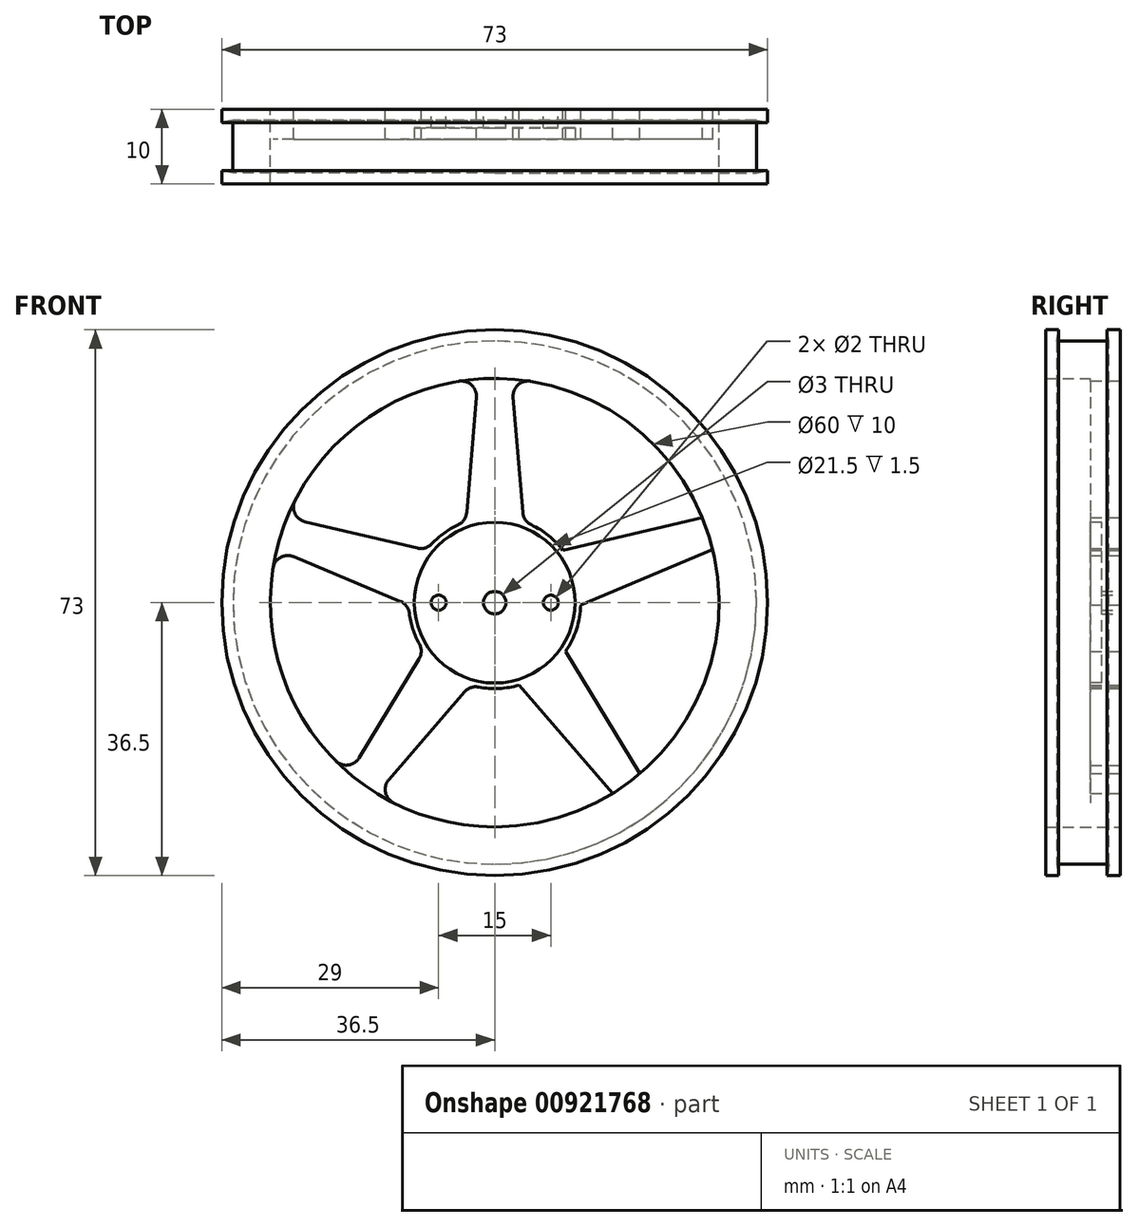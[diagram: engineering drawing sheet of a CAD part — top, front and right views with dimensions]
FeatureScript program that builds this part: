
annotation { "Feature Type Name" : "Feature", "Feature Type Description" : "" }
export const myFeature = defineFeature(function(context is Context, id is Id, definition is map)
    precondition{}
    {
        {
            var Q0;
            Q0=qCreatedBy(makeId("Front.planeOp"),FACE);
            var sketch = newSketch(context, id + "F0", { "sketchPlane" : qUnion([Q0])});
            skCircle(sketch, "E0", {"center": v(0, 0) * mm, "radius": 36.5 * mm});
            skCircle(sketch, "E1", {"center": v(0, 0) * mm, "radius": 30 * mm});
            skSolve(sketch);
        }
        {
            var Q0;
            Q0 = qSketchRegion(id + "F0", true);
            extrude(context, id + "F1", {"entities" : qUnion([Q0]), "depth" : 10 * mm, "offsetDistance" : 25 * mm});
        }
        {
            var Q0;
            Q0=qCreatedBy(makeId("Front.planeOp"),FACE);
            var sketch = newSketch(context, id + "F2", { "sketchPlane" : qUnion([Q0])});
            skCircle(sketch, "E2", {"center": v(0, 0) * mm, "radius": 11.5 * mm});
            skCircle(sketch, "E3", {"center": v(0, 0) * mm, "radius": 1.5 * mm});
            skCircle(sketch, "E4", {"center": v(-7.5, 0) * mm, "radius": 1 * mm});
            skCircle(sketch, "E5", {"center": v(7.5, 0) * mm, "radius": 1 * mm});
            skSolve(sketch);
        }
        {
            var Q0;
            Q0=makeQuery(id+"F2.imprint","IMPRINT",FACE,{"disambiguationData":[TD([[makeQuery(id+"F2.imprint","IMPRINT",EDGE,{"derivedFrom":sQuery(id+"F2.wireOp",EDGE,"E2")}),1.0]])]});
            extrude(context, id + "F3", {"entities" : qUnion([Q0]), "operationType" : NewBodyOperationType.ADD, "depth" : 4 * mm, "offsetDistance" : 25 * mm});
        }
        {
            var Q0;
            Q0=qCreatedBy(makeId("Front.planeOp"),FACE);
            var sketch = newSketch(context, id + "F4", { "sketchPlane" : qUnion([Q0])});
            skLineSegment(sketch, "E6", {"start": v(-4, 9) * mm, "end": v(4, 9) * mm});
            skLineSegment(sketch, "E7", {"start": v(2, 33) * mm, "end": v(-2, 33) * mm});
            skLineSegment(sketch, "E8", {"start": v(-2, 33) * mm, "end": v(-4, 9) * mm});
            skLineSegment(sketch, "E9", {"start": v(2, 33) * mm, "end": v(4, 9) * mm});
            skLineSegment(sketch, "E10.1.0", {"start": v(-32, 8.3) * mm, "end": v(-9.8, -1.02) * mm});
            skLineSegment(sketch, "E10.1.1", {"start": v(-30.77, 12.1) * mm, "end": v(-32, 8.3) * mm});
            skLineSegment(sketch, "E10.1.2", {"start": v(-30.77, 12.1) * mm, "end": v(-7.32, 6.59) * mm});
            skLineSegment(sketch, "E10.1.3", {"start": v(-9.8, -1.02) * mm, "end": v(-7.32, 6.59) * mm});
            skLineSegment(sketch, "E10.2.0", {"start": v(-17.78, -27.87) * mm, "end": v(-2.05, -9.63) * mm});
            skLineSegment(sketch, "E10.2.1", {"start": v(-21.01, -25.52) * mm, "end": v(-17.78, -27.87) * mm});
            skLineSegment(sketch, "E10.2.2", {"start": v(-21.01, -25.52) * mm, "end": v(-8.53, -4.93) * mm});
            skLineSegment(sketch, "E10.2.3", {"start": v(-2.05, -9.63) * mm, "end": v(-8.53, -4.93) * mm});
            skPoint(sketch, "E10.center", {"position": v(0, 0) * mm});
            skLineSegment(sketch, "E11.2.3.0", {"start": v(21.01, -25.52) * mm, "end": v(8.53, -4.93) * mm});
            skLineSegment(sketch, "E11.3.3.0", {"start": v(17.78, -27.87) * mm, "end": v(21.01, -25.52) * mm});
            skLineSegment(sketch, "E11.6.3.0", {"start": v(17.78, -27.87) * mm, "end": v(2.05, -9.63) * mm});
            skLineSegment(sketch, "E11.9.3.0", {"start": v(8.53, -4.93) * mm, "end": v(2.05, -9.63) * mm});
            skLineSegment(sketch, "E12.2.4.0", {"start": v(30.77, 12.1) * mm, "end": v(7.32, 6.59) * mm});
            skLineSegment(sketch, "E12.3.4.0", {"start": v(32, 8.3) * mm, "end": v(30.77, 12.1) * mm});
            skLineSegment(sketch, "E12.6.4.0", {"start": v(32, 8.3) * mm, "end": v(9.8, -1.02) * mm});
            skLineSegment(sketch, "E12.9.4.0", {"start": v(7.32, 6.59) * mm, "end": v(9.8, -1.02) * mm});
            skSolve(sketch);
        }
        {
            var Q0;
            Q0 = qSketchRegion(id + "F4", true);
            extrude(context, id + "F5", {"entities" : qUnion([Q0]), "operationType" : NewBodyOperationType.ADD, "depth" : 4 * mm, "offsetDistance" : 25 * mm});
        }
        {
            var Q0;
            Q0=makeQuery(id+"F5.boolean.opBoolean","INTERSECT",EDGE,{"disambiguationData":[OD(0.0)],"derivedFrom":[makeQuery(id+"F1.opExtrude","SWEPT_FACE",FACE,{"disambiguationData":[OSD([sQuery(id+"F0.wireOp",EDGE,"E1")])]}),makeQuery(id+"F5.opExtrude","CAP_FACE",FACE,{"disambiguationData":[OSD([sQuery(id+"F4.wireOp",EDGE,"E6"),sQuery(id+"F4.wireOp",EDGE,"E7"),sQuery(id+"F4.wireOp",EDGE,"E8"),sQuery(id+"F4.wireOp",EDGE,"E9"),sQuery(id+"F4.wireOp",EDGE,"E10.1.0"),sQuery(id+"F4.wireOp",EDGE,"E10.1.1"),sQuery(id+"F4.wireOp",EDGE,"E10.1.2"),sQuery(id+"F4.wireOp",EDGE,"E10.1.3"),sQuery(id+"F4.wireOp",EDGE,"E10.2.0"),sQuery(id+"F4.wireOp",EDGE,"E10.2.1"),sQuery(id+"F4.wireOp",EDGE,"E10.2.2"),sQuery(id+"F4.wireOp",EDGE,"E10.2.3"),sQuery(id+"F4.wireOp",EDGE,"E10.3.0"),sQuery(id+"F4.wireOp",EDGE,"E10.3.1"),sQuery(id+"F4.wireOp",EDGE,"E10.3.2"),sQuery(id+"F4.wireOp",EDGE,"E10.3.3"),sQuery(id+"F4.wireOp",EDGE,"E10.4.0"),sQuery(id+"F4.wireOp",EDGE,"E10.4.1"),sQuery(id+"F4.wireOp",EDGE,"E10.4.2"),sQuery(id+"F4.wireOp",EDGE,"E10.4.3"),sQuery(id+"F4.wireOp",EDGE,"E10.5.0"),sQuery(id+"F4.wireOp",EDGE,"E10.5.1"),sQuery(id+"F4.wireOp",EDGE,"E10.5.2"),sQuery(id+"F4.wireOp",EDGE,"E10.5.3"),sQuery(id+"F4.wireOp",EDGE,"E10.6.0"),sQuery(id+"F4.wireOp",EDGE,"E10.6.1"),sQuery(id+"F4.wireOp",EDGE,"E10.6.2"),sQuery(id+"F4.wireOp",EDGE,"E10.6.3")])],"isStart":false})]});
            var Q1;
            Q1=makeQuery(id+"F5.boolean.opBoolean","INTERSECT",EDGE,{"disambiguationData":[OD(1.0)],"derivedFrom":[makeQuery(id+"F1.opExtrude","SWEPT_FACE",FACE,{"disambiguationData":[OSD([sQuery(id+"F0.wireOp",EDGE,"E1")])]}),makeQuery(id+"F5.opExtrude","CAP_FACE",FACE,{"disambiguationData":[OSD([sQuery(id+"F4.wireOp",EDGE,"E6"),sQuery(id+"F4.wireOp",EDGE,"E7"),sQuery(id+"F4.wireOp",EDGE,"E8"),sQuery(id+"F4.wireOp",EDGE,"E9"),sQuery(id+"F4.wireOp",EDGE,"E10.1.0"),sQuery(id+"F4.wireOp",EDGE,"E10.1.1"),sQuery(id+"F4.wireOp",EDGE,"E10.1.2"),sQuery(id+"F4.wireOp",EDGE,"E10.1.3"),sQuery(id+"F4.wireOp",EDGE,"E10.2.0"),sQuery(id+"F4.wireOp",EDGE,"E10.2.1"),sQuery(id+"F4.wireOp",EDGE,"E10.2.2"),sQuery(id+"F4.wireOp",EDGE,"E10.2.3"),sQuery(id+"F4.wireOp",EDGE,"E10.3.0"),sQuery(id+"F4.wireOp",EDGE,"E10.3.1"),sQuery(id+"F4.wireOp",EDGE,"E10.3.2"),sQuery(id+"F4.wireOp",EDGE,"E10.3.3"),sQuery(id+"F4.wireOp",EDGE,"E10.4.0"),sQuery(id+"F4.wireOp",EDGE,"E10.4.1"),sQuery(id+"F4.wireOp",EDGE,"E10.4.2"),sQuery(id+"F4.wireOp",EDGE,"E10.4.3"),sQuery(id+"F4.wireOp",EDGE,"E10.5.0"),sQuery(id+"F4.wireOp",EDGE,"E10.5.1"),sQuery(id+"F4.wireOp",EDGE,"E10.5.2"),sQuery(id+"F4.wireOp",EDGE,"E10.5.3"),sQuery(id+"F4.wireOp",EDGE,"E10.6.0"),sQuery(id+"F4.wireOp",EDGE,"E10.6.1"),sQuery(id+"F4.wireOp",EDGE,"E10.6.2"),sQuery(id+"F4.wireOp",EDGE,"E10.6.3")])],"isStart":false})]});
            var Q2;
            Q2=makeQuery(id+"F5.boolean.opBoolean","INTERSECT",EDGE,{"disambiguationData":[OD(2.0)],"derivedFrom":[makeQuery(id+"F1.opExtrude","SWEPT_FACE",FACE,{"disambiguationData":[OSD([sQuery(id+"F0.wireOp",EDGE,"E1")])]}),makeQuery(id+"F5.opExtrude","CAP_FACE",FACE,{"disambiguationData":[OSD([sQuery(id+"F4.wireOp",EDGE,"E6"),sQuery(id+"F4.wireOp",EDGE,"E7"),sQuery(id+"F4.wireOp",EDGE,"E8"),sQuery(id+"F4.wireOp",EDGE,"E9"),sQuery(id+"F4.wireOp",EDGE,"E10.1.0"),sQuery(id+"F4.wireOp",EDGE,"E10.1.1"),sQuery(id+"F4.wireOp",EDGE,"E10.1.2"),sQuery(id+"F4.wireOp",EDGE,"E10.1.3"),sQuery(id+"F4.wireOp",EDGE,"E10.2.0"),sQuery(id+"F4.wireOp",EDGE,"E10.2.1"),sQuery(id+"F4.wireOp",EDGE,"E10.2.2"),sQuery(id+"F4.wireOp",EDGE,"E10.2.3"),sQuery(id+"F4.wireOp",EDGE,"E10.3.0"),sQuery(id+"F4.wireOp",EDGE,"E10.3.1"),sQuery(id+"F4.wireOp",EDGE,"E10.3.2"),sQuery(id+"F4.wireOp",EDGE,"E10.3.3"),sQuery(id+"F4.wireOp",EDGE,"E10.4.0"),sQuery(id+"F4.wireOp",EDGE,"E10.4.1"),sQuery(id+"F4.wireOp",EDGE,"E10.4.2"),sQuery(id+"F4.wireOp",EDGE,"E10.4.3"),sQuery(id+"F4.wireOp",EDGE,"E10.5.0"),sQuery(id+"F4.wireOp",EDGE,"E10.5.1"),sQuery(id+"F4.wireOp",EDGE,"E10.5.2"),sQuery(id+"F4.wireOp",EDGE,"E10.5.3"),sQuery(id+"F4.wireOp",EDGE,"E10.6.0"),sQuery(id+"F4.wireOp",EDGE,"E10.6.1"),sQuery(id+"F4.wireOp",EDGE,"E10.6.2"),sQuery(id+"F4.wireOp",EDGE,"E10.6.3")])],"isStart":false})]});
            var Q3;
            Q3=makeQuery(id+"F5.boolean.opBoolean","INTERSECT",EDGE,{"disambiguationData":[OD(3.0)],"derivedFrom":[makeQuery(id+"F1.opExtrude","SWEPT_FACE",FACE,{"disambiguationData":[OSD([sQuery(id+"F0.wireOp",EDGE,"E1")])]}),makeQuery(id+"F5.opExtrude","CAP_FACE",FACE,{"disambiguationData":[OSD([sQuery(id+"F4.wireOp",EDGE,"E6"),sQuery(id+"F4.wireOp",EDGE,"E7"),sQuery(id+"F4.wireOp",EDGE,"E8"),sQuery(id+"F4.wireOp",EDGE,"E9"),sQuery(id+"F4.wireOp",EDGE,"E10.1.0"),sQuery(id+"F4.wireOp",EDGE,"E10.1.1"),sQuery(id+"F4.wireOp",EDGE,"E10.1.2"),sQuery(id+"F4.wireOp",EDGE,"E10.1.3"),sQuery(id+"F4.wireOp",EDGE,"E10.2.0"),sQuery(id+"F4.wireOp",EDGE,"E10.2.1"),sQuery(id+"F4.wireOp",EDGE,"E10.2.2"),sQuery(id+"F4.wireOp",EDGE,"E10.2.3"),sQuery(id+"F4.wireOp",EDGE,"E10.3.0"),sQuery(id+"F4.wireOp",EDGE,"E10.3.1"),sQuery(id+"F4.wireOp",EDGE,"E10.3.2"),sQuery(id+"F4.wireOp",EDGE,"E10.3.3"),sQuery(id+"F4.wireOp",EDGE,"E10.4.0"),sQuery(id+"F4.wireOp",EDGE,"E10.4.1"),sQuery(id+"F4.wireOp",EDGE,"E10.4.2"),sQuery(id+"F4.wireOp",EDGE,"E10.4.3"),sQuery(id+"F4.wireOp",EDGE,"E10.5.0"),sQuery(id+"F4.wireOp",EDGE,"E10.5.1"),sQuery(id+"F4.wireOp",EDGE,"E10.5.2"),sQuery(id+"F4.wireOp",EDGE,"E10.5.3"),sQuery(id+"F4.wireOp",EDGE,"E10.6.0"),sQuery(id+"F4.wireOp",EDGE,"E10.6.1"),sQuery(id+"F4.wireOp",EDGE,"E10.6.2"),sQuery(id+"F4.wireOp",EDGE,"E10.6.3")])],"isStart":false})]});
            var Q4;
            Q4=makeQuery(id+"F5.boolean.opBoolean","INTERSECT",EDGE,{"disambiguationData":[OD(4.0)],"derivedFrom":[makeQuery(id+"F1.opExtrude","SWEPT_FACE",FACE,{"disambiguationData":[OSD([sQuery(id+"F0.wireOp",EDGE,"E1")])]}),makeQuery(id+"F5.opExtrude","CAP_FACE",FACE,{"disambiguationData":[OSD([sQuery(id+"F4.wireOp",EDGE,"E6"),sQuery(id+"F4.wireOp",EDGE,"E7"),sQuery(id+"F4.wireOp",EDGE,"E8"),sQuery(id+"F4.wireOp",EDGE,"E9"),sQuery(id+"F4.wireOp",EDGE,"E10.1.0"),sQuery(id+"F4.wireOp",EDGE,"E10.1.1"),sQuery(id+"F4.wireOp",EDGE,"E10.1.2"),sQuery(id+"F4.wireOp",EDGE,"E10.1.3"),sQuery(id+"F4.wireOp",EDGE,"E10.2.0"),sQuery(id+"F4.wireOp",EDGE,"E10.2.1"),sQuery(id+"F4.wireOp",EDGE,"E10.2.2"),sQuery(id+"F4.wireOp",EDGE,"E10.2.3"),sQuery(id+"F4.wireOp",EDGE,"E10.3.0"),sQuery(id+"F4.wireOp",EDGE,"E10.3.1"),sQuery(id+"F4.wireOp",EDGE,"E10.3.2"),sQuery(id+"F4.wireOp",EDGE,"E10.3.3"),sQuery(id+"F4.wireOp",EDGE,"E10.4.0"),sQuery(id+"F4.wireOp",EDGE,"E10.4.1"),sQuery(id+"F4.wireOp",EDGE,"E10.4.2"),sQuery(id+"F4.wireOp",EDGE,"E10.4.3"),sQuery(id+"F4.wireOp",EDGE,"E10.5.0"),sQuery(id+"F4.wireOp",EDGE,"E10.5.1"),sQuery(id+"F4.wireOp",EDGE,"E10.5.2"),sQuery(id+"F4.wireOp",EDGE,"E10.5.3"),sQuery(id+"F4.wireOp",EDGE,"E10.6.0"),sQuery(id+"F4.wireOp",EDGE,"E10.6.1"),sQuery(id+"F4.wireOp",EDGE,"E10.6.2"),sQuery(id+"F4.wireOp",EDGE,"E10.6.3")])],"isStart":false})]});
            var Q5;
            Q5=makeQuery(id+"F5.boolean.opBoolean","INTERSECT",EDGE,{"disambiguationData":[OD(5.0)],"derivedFrom":[makeQuery(id+"F1.opExtrude","SWEPT_FACE",FACE,{"disambiguationData":[OSD([sQuery(id+"F0.wireOp",EDGE,"E1")])]}),makeQuery(id+"F5.opExtrude","CAP_FACE",FACE,{"disambiguationData":[OSD([sQuery(id+"F4.wireOp",EDGE,"E6"),sQuery(id+"F4.wireOp",EDGE,"E7"),sQuery(id+"F4.wireOp",EDGE,"E8"),sQuery(id+"F4.wireOp",EDGE,"E9"),sQuery(id+"F4.wireOp",EDGE,"E10.1.0"),sQuery(id+"F4.wireOp",EDGE,"E10.1.1"),sQuery(id+"F4.wireOp",EDGE,"E10.1.2"),sQuery(id+"F4.wireOp",EDGE,"E10.1.3"),sQuery(id+"F4.wireOp",EDGE,"E10.2.0"),sQuery(id+"F4.wireOp",EDGE,"E10.2.1"),sQuery(id+"F4.wireOp",EDGE,"E10.2.2"),sQuery(id+"F4.wireOp",EDGE,"E10.2.3"),sQuery(id+"F4.wireOp",EDGE,"E10.3.0"),sQuery(id+"F4.wireOp",EDGE,"E10.3.1"),sQuery(id+"F4.wireOp",EDGE,"E10.3.2"),sQuery(id+"F4.wireOp",EDGE,"E10.3.3"),sQuery(id+"F4.wireOp",EDGE,"E10.4.0"),sQuery(id+"F4.wireOp",EDGE,"E10.4.1"),sQuery(id+"F4.wireOp",EDGE,"E10.4.2"),sQuery(id+"F4.wireOp",EDGE,"E10.4.3"),sQuery(id+"F4.wireOp",EDGE,"E10.5.0"),sQuery(id+"F4.wireOp",EDGE,"E10.5.1"),sQuery(id+"F4.wireOp",EDGE,"E10.5.2"),sQuery(id+"F4.wireOp",EDGE,"E10.5.3"),sQuery(id+"F4.wireOp",EDGE,"E10.6.0"),sQuery(id+"F4.wireOp",EDGE,"E10.6.1"),sQuery(id+"F4.wireOp",EDGE,"E10.6.2"),sQuery(id+"F4.wireOp",EDGE,"E10.6.3")])],"isStart":false})]});
            var Q6;
            Q6=makeQuery(id+"F5.boolean.opBoolean","INTERSECT",EDGE,{"disambiguationData":[OD(6.0)],"derivedFrom":[makeQuery(id+"F1.opExtrude","SWEPT_FACE",FACE,{"disambiguationData":[OSD([sQuery(id+"F0.wireOp",EDGE,"E1")])]}),makeQuery(id+"F5.opExtrude","CAP_FACE",FACE,{"disambiguationData":[OSD([sQuery(id+"F4.wireOp",EDGE,"E6"),sQuery(id+"F4.wireOp",EDGE,"E7"),sQuery(id+"F4.wireOp",EDGE,"E8"),sQuery(id+"F4.wireOp",EDGE,"E9"),sQuery(id+"F4.wireOp",EDGE,"E10.1.0"),sQuery(id+"F4.wireOp",EDGE,"E10.1.1"),sQuery(id+"F4.wireOp",EDGE,"E10.1.2"),sQuery(id+"F4.wireOp",EDGE,"E10.1.3"),sQuery(id+"F4.wireOp",EDGE,"E10.2.0"),sQuery(id+"F4.wireOp",EDGE,"E10.2.1"),sQuery(id+"F4.wireOp",EDGE,"E10.2.2"),sQuery(id+"F4.wireOp",EDGE,"E10.2.3"),sQuery(id+"F4.wireOp",EDGE,"E10.3.0"),sQuery(id+"F4.wireOp",EDGE,"E10.3.1"),sQuery(id+"F4.wireOp",EDGE,"E10.3.2"),sQuery(id+"F4.wireOp",EDGE,"E10.3.3"),sQuery(id+"F4.wireOp",EDGE,"E10.4.0"),sQuery(id+"F4.wireOp",EDGE,"E10.4.1"),sQuery(id+"F4.wireOp",EDGE,"E10.4.2"),sQuery(id+"F4.wireOp",EDGE,"E10.4.3"),sQuery(id+"F4.wireOp",EDGE,"E10.5.0"),sQuery(id+"F4.wireOp",EDGE,"E10.5.1"),sQuery(id+"F4.wireOp",EDGE,"E10.5.2"),sQuery(id+"F4.wireOp",EDGE,"E10.5.3"),sQuery(id+"F4.wireOp",EDGE,"E10.6.0"),sQuery(id+"F4.wireOp",EDGE,"E10.6.1"),sQuery(id+"F4.wireOp",EDGE,"E10.6.2"),sQuery(id+"F4.wireOp",EDGE,"E10.6.3")])],"isStart":false})]});
            var Q7;
            Q7=makeQuery(id+"F5.boolean.opBoolean","INTERSECT",EDGE,{"derivedFrom":[makeQuery(id+"F1.opExtrude","SWEPT_FACE",FACE,{"disambiguationData":[OSD([sQuery(id+"F0.wireOp",EDGE,"E1")])]}),makeQuery(id+"F5.opExtrude","SWEPT_FACE",FACE,{"disambiguationData":[OSD([sQuery(id+"F4.wireOp",EDGE,"E9")])]})]});
            var Q8;
            Q8=makeQuery(id+"F5.boolean.opBoolean","INTERSECT",EDGE,{"derivedFrom":[makeQuery(id+"F1.opExtrude","SWEPT_FACE",FACE,{"disambiguationData":[OSD([sQuery(id+"F0.wireOp",EDGE,"E1")])]}),makeQuery(id+"F5.opExtrude","SWEPT_FACE",FACE,{"disambiguationData":[OSD([sQuery(id+"F4.wireOp",EDGE,"E8")])]})]});
            var Q9;
            Q9=makeQuery(id+"F5.boolean.opBoolean","INTERSECT",EDGE,{"derivedFrom":[makeQuery(id+"F1.opExtrude","SWEPT_FACE",FACE,{"disambiguationData":[OSD([sQuery(id+"F0.wireOp",EDGE,"E1")])]}),makeQuery(id+"F5.opExtrude","SWEPT_FACE",FACE,{"disambiguationData":[OSD([sQuery(id+"F4.wireOp",EDGE,"E10.6.0")])]})]});
            var Q10;
            Q10=makeQuery(id+"F5.boolean.opBoolean","INTERSECT",EDGE,{"derivedFrom":[makeQuery(id+"F1.opExtrude","SWEPT_FACE",FACE,{"disambiguationData":[OSD([sQuery(id+"F0.wireOp",EDGE,"E1")])]}),makeQuery(id+"F5.opExtrude","SWEPT_FACE",FACE,{"disambiguationData":[OSD([sQuery(id+"F4.wireOp",EDGE,"E10.6.2")])]})]});
            var Q11;
            Q11=makeQuery(id+"F5.boolean.opBoolean","INTERSECT",EDGE,{"derivedFrom":[makeQuery(id+"F1.opExtrude","SWEPT_FACE",FACE,{"disambiguationData":[OSD([sQuery(id+"F0.wireOp",EDGE,"E1")])]}),makeQuery(id+"F5.opExtrude","SWEPT_FACE",FACE,{"disambiguationData":[OSD([sQuery(id+"F4.wireOp",EDGE,"E10.5.0")])]})]});
            var Q12;
            Q12=makeQuery(id+"F5.boolean.opBoolean","INTERSECT",EDGE,{"derivedFrom":[makeQuery(id+"F1.opExtrude","SWEPT_FACE",FACE,{"disambiguationData":[OSD([sQuery(id+"F0.wireOp",EDGE,"E1")])]}),makeQuery(id+"F5.opExtrude","SWEPT_FACE",FACE,{"disambiguationData":[OSD([sQuery(id+"F4.wireOp",EDGE,"E10.5.2")])]})]});
            var Q13;
            Q13=makeQuery(id+"F5.boolean.opBoolean","INTERSECT",EDGE,{"derivedFrom":[makeQuery(id+"F1.opExtrude","SWEPT_FACE",FACE,{"disambiguationData":[OSD([sQuery(id+"F0.wireOp",EDGE,"E1")])]}),makeQuery(id+"F5.opExtrude","SWEPT_FACE",FACE,{"disambiguationData":[OSD([sQuery(id+"F4.wireOp",EDGE,"E10.4.0")])]})]});
            var Q14;
            Q14=makeQuery(id+"F5.boolean.opBoolean","INTERSECT",EDGE,{"derivedFrom":[makeQuery(id+"F1.opExtrude","SWEPT_FACE",FACE,{"disambiguationData":[OSD([sQuery(id+"F0.wireOp",EDGE,"E1")])]}),makeQuery(id+"F5.opExtrude","SWEPT_FACE",FACE,{"disambiguationData":[OSD([sQuery(id+"F4.wireOp",EDGE,"E10.4.2")])]})]});
            var Q15;
            Q15=makeQuery(id+"F5.boolean.opBoolean","INTERSECT",EDGE,{"derivedFrom":[makeQuery(id+"F1.opExtrude","SWEPT_FACE",FACE,{"disambiguationData":[OSD([sQuery(id+"F0.wireOp",EDGE,"E1")])]}),makeQuery(id+"F5.opExtrude","SWEPT_FACE",FACE,{"disambiguationData":[OSD([sQuery(id+"F4.wireOp",EDGE,"E10.2.0")])]})]});
            var Q16;
            Q16=makeQuery(id+"F5.boolean.opBoolean","INTERSECT",EDGE,{"derivedFrom":[makeQuery(id+"F1.opExtrude","SWEPT_FACE",FACE,{"disambiguationData":[OSD([sQuery(id+"F0.wireOp",EDGE,"E1")])]}),makeQuery(id+"F5.opExtrude","SWEPT_FACE",FACE,{"disambiguationData":[OSD([sQuery(id+"F4.wireOp",EDGE,"E10.3.0")])]})]});
            var Q17;
            Q17=makeQuery(id+"F5.boolean.opBoolean","INTERSECT",EDGE,{"derivedFrom":[makeQuery(id+"F1.opExtrude","SWEPT_FACE",FACE,{"disambiguationData":[OSD([sQuery(id+"F0.wireOp",EDGE,"E1")])]}),makeQuery(id+"F5.opExtrude","SWEPT_FACE",FACE,{"disambiguationData":[OSD([sQuery(id+"F4.wireOp",EDGE,"E10.1.2")])]})]});
            var Q18;
            Q18=makeQuery(id+"F5.boolean.opBoolean","INTERSECT",EDGE,{"derivedFrom":[makeQuery(id+"F1.opExtrude","SWEPT_FACE",FACE,{"disambiguationData":[OSD([sQuery(id+"F0.wireOp",EDGE,"E1")])]}),makeQuery(id+"F5.opExtrude","SWEPT_FACE",FACE,{"disambiguationData":[OSD([sQuery(id+"F4.wireOp",EDGE,"E10.1.0")])]})]});
            var Q19;
            Q19=makeQuery(id+"F5.boolean.opBoolean","INTERSECT",EDGE,{"derivedFrom":[makeQuery(id+"F1.opExtrude","SWEPT_FACE",FACE,{"disambiguationData":[OSD([sQuery(id+"F0.wireOp",EDGE,"E1")])]}),makeQuery(id+"F5.opExtrude","SWEPT_FACE",FACE,{"disambiguationData":[OSD([sQuery(id+"F4.wireOp",EDGE,"E10.2.2")])]})]});
            var Q20;
            Q20=makeQuery(id+"F5.boolean.opBoolean","INTERSECT",EDGE,{"derivedFrom":[makeQuery(id+"F1.opExtrude","SWEPT_FACE",FACE,{"disambiguationData":[OSD([sQuery(id+"F0.wireOp",EDGE,"E1")])]}),makeQuery(id+"F5.opExtrude","SWEPT_FACE",FACE,{"disambiguationData":[OSD([sQuery(id+"F4.wireOp",EDGE,"E10.3.2")])]})]});
            var Q21;
            Q21=makeQuery(id+"F5.boolean.opBoolean","INTERSECT",EDGE,{"derivedFrom":[makeQuery(id+"F3.opExtrude","SWEPT_FACE",FACE,{"disambiguationData":[OSD([sQuery(id+"F2.wireOp",EDGE,"E2")])]}),makeQuery(id+"F5.opExtrude","SWEPT_FACE",FACE,{"disambiguationData":[OSD([sQuery(id+"F4.wireOp",EDGE,"E10.3.2")])]})]});
            var Q22;
            Q22=makeQuery(id+"F5.boolean.opBoolean","INTERSECT",EDGE,{"derivedFrom":[makeQuery(id+"F3.opExtrude","SWEPT_FACE",FACE,{"disambiguationData":[OSD([sQuery(id+"F2.wireOp",EDGE,"E2")])]}),makeQuery(id+"F5.opExtrude","SWEPT_FACE",FACE,{"disambiguationData":[OSD([sQuery(id+"F4.wireOp",EDGE,"E10.2.0")])]})]});
            var Q23;
            Q23=makeQuery(id+"F5.boolean.opBoolean","INTERSECT",EDGE,{"derivedFrom":[makeQuery(id+"F3.opExtrude","SWEPT_FACE",FACE,{"disambiguationData":[OSD([sQuery(id+"F2.wireOp",EDGE,"E2")])]}),makeQuery(id+"F5.opExtrude","SWEPT_FACE",FACE,{"disambiguationData":[OSD([sQuery(id+"F4.wireOp",EDGE,"E10.2.2")])]})]});
            var Q24;
            Q24=makeQuery(id+"F5.boolean.opBoolean","INTERSECT",EDGE,{"derivedFrom":[makeQuery(id+"F3.opExtrude","SWEPT_FACE",FACE,{"disambiguationData":[OSD([sQuery(id+"F2.wireOp",EDGE,"E2")])]}),makeQuery(id+"F5.opExtrude","SWEPT_FACE",FACE,{"disambiguationData":[OSD([sQuery(id+"F4.wireOp",EDGE,"E10.1.0")])]})]});
            var Q25;
            Q25=makeQuery(id+"F5.boolean.opBoolean","INTERSECT",EDGE,{"derivedFrom":[makeQuery(id+"F3.opExtrude","SWEPT_FACE",FACE,{"disambiguationData":[OSD([sQuery(id+"F2.wireOp",EDGE,"E2")])]}),makeQuery(id+"F5.opExtrude","SWEPT_FACE",FACE,{"disambiguationData":[OSD([sQuery(id+"F4.wireOp",EDGE,"E10.1.2")])]})]});
            var Q26;
            Q26=makeQuery(id+"F5.boolean.opBoolean","INTERSECT",EDGE,{"derivedFrom":[makeQuery(id+"F3.opExtrude","SWEPT_FACE",FACE,{"disambiguationData":[OSD([sQuery(id+"F2.wireOp",EDGE,"E2")])]}),makeQuery(id+"F5.opExtrude","SWEPT_FACE",FACE,{"disambiguationData":[OSD([sQuery(id+"F4.wireOp",EDGE,"E8")])]})]});
            var Q27;
            Q27=makeQuery(id+"F5.boolean.opBoolean","INTERSECT",EDGE,{"derivedFrom":[makeQuery(id+"F3.opExtrude","SWEPT_FACE",FACE,{"disambiguationData":[OSD([sQuery(id+"F2.wireOp",EDGE,"E2")])]}),makeQuery(id+"F5.opExtrude","SWEPT_FACE",FACE,{"disambiguationData":[OSD([sQuery(id+"F4.wireOp",EDGE,"E10.6.0")])]})]});
            var Q28;
            Q28=makeQuery(id+"F5.boolean.opBoolean","INTERSECT",EDGE,{"derivedFrom":[makeQuery(id+"F3.opExtrude","SWEPT_FACE",FACE,{"disambiguationData":[OSD([sQuery(id+"F2.wireOp",EDGE,"E2")])]}),makeQuery(id+"F5.opExtrude","SWEPT_FACE",FACE,{"disambiguationData":[OSD([sQuery(id+"F4.wireOp",EDGE,"E9")])]})]});
            var Q29;
            Q29=makeQuery(id+"F5.boolean.opBoolean","INTERSECT",EDGE,{"derivedFrom":[makeQuery(id+"F3.opExtrude","SWEPT_FACE",FACE,{"disambiguationData":[OSD([sQuery(id+"F2.wireOp",EDGE,"E2")])]}),makeQuery(id+"F5.opExtrude","SWEPT_FACE",FACE,{"disambiguationData":[OSD([sQuery(id+"F4.wireOp",EDGE,"E10.6.2")])]})]});
            var Q30;
            Q30=makeQuery(id+"F5.boolean.opBoolean","INTERSECT",EDGE,{"derivedFrom":[makeQuery(id+"F3.opExtrude","SWEPT_FACE",FACE,{"disambiguationData":[OSD([sQuery(id+"F2.wireOp",EDGE,"E2")])]}),makeQuery(id+"F5.opExtrude","SWEPT_FACE",FACE,{"disambiguationData":[OSD([sQuery(id+"F4.wireOp",EDGE,"E10.5.0")])]})]});
            var Q31;
            Q31=makeQuery(id+"F5.boolean.opBoolean","INTERSECT",EDGE,{"derivedFrom":[makeQuery(id+"F3.opExtrude","SWEPT_FACE",FACE,{"disambiguationData":[OSD([sQuery(id+"F2.wireOp",EDGE,"E2")])]}),makeQuery(id+"F5.opExtrude","SWEPT_FACE",FACE,{"disambiguationData":[OSD([sQuery(id+"F4.wireOp",EDGE,"E10.4.0")])]})]});
            var Q32;
            Q32=makeQuery(id+"F5.boolean.opBoolean","INTERSECT",EDGE,{"derivedFrom":[makeQuery(id+"F3.opExtrude","SWEPT_FACE",FACE,{"disambiguationData":[OSD([sQuery(id+"F2.wireOp",EDGE,"E2")])]}),makeQuery(id+"F5.opExtrude","SWEPT_FACE",FACE,{"disambiguationData":[OSD([sQuery(id+"F4.wireOp",EDGE,"E10.5.2")])]})]});
            var Q33;
            Q33=makeQuery(id+"F5.boolean.opBoolean","INTERSECT",EDGE,{"derivedFrom":[makeQuery(id+"F3.opExtrude","SWEPT_FACE",FACE,{"disambiguationData":[OSD([sQuery(id+"F2.wireOp",EDGE,"E2")])]}),makeQuery(id+"F5.opExtrude","SWEPT_FACE",FACE,{"disambiguationData":[OSD([sQuery(id+"F4.wireOp",EDGE,"E10.3.0")])]})]});
            var Q34;
            Q34=makeQuery(id+"F5.boolean.opBoolean","INTERSECT",EDGE,{"derivedFrom":[makeQuery(id+"F3.opExtrude","SWEPT_FACE",FACE,{"disambiguationData":[OSD([sQuery(id+"F2.wireOp",EDGE,"E2")])]}),makeQuery(id+"F5.opExtrude","SWEPT_FACE",FACE,{"disambiguationData":[OSD([sQuery(id+"F4.wireOp",EDGE,"E10.4.2")])]})]});
            fillet(context, id + "F6", {"entities" : qUnion([Q0, Q1, Q2, Q3, Q4, Q5, Q6, Q7, Q8, Q9, Q10, Q11, Q12, Q13, Q14, Q15, Q16, Q17, Q18, Q19, Q20, Q21, Q22, Q23, Q24, Q25, Q26, Q27, Q28, Q29, Q30, Q31, Q32, Q33, Q34]), "radius" : 2 * mm, "tangentPropagation" : true, "allowEdgeOverflow" : false});
        }
        {
            var Q0;
            Q0=makeQuery(id+"F5.boolean.opBoolean","MERGE",FACE,{"derivedFrom":[makeQuery(id+"F3.opExtrude","CAP_FACE",FACE,{"disambiguationData":[OSD([sQuery(id+"F2.wireOp",EDGE,"E2"),sQuery(id+"F2.wireOp",EDGE,"E3"),sQuery(id+"F2.wireOp",EDGE,"E4"),sQuery(id+"F2.wireOp",EDGE,"E5")])],"isStart":false}),makeQuery(id+"F5.opExtrude","CAP_FACE",FACE,{"disambiguationData":[OSD([sQuery(id+"F4.wireOp",EDGE,"E6"),sQuery(id+"F4.wireOp",EDGE,"E7"),sQuery(id+"F4.wireOp",EDGE,"E8"),sQuery(id+"F4.wireOp",EDGE,"E9")])],"isStart":false}),makeQuery(id+"F5.opExtrude","CAP_FACE",FACE,{"disambiguationData":[OSD([sQuery(id+"F4.wireOp",EDGE,"E10.1.0"),sQuery(id+"F4.wireOp",EDGE,"E10.1.1"),sQuery(id+"F4.wireOp",EDGE,"E10.1.2"),sQuery(id+"F4.wireOp",EDGE,"E10.1.3")])],"isStart":false}),makeQuery(id+"F5.opExtrude","CAP_FACE",FACE,{"disambiguationData":[OSD([sQuery(id+"F4.wireOp",EDGE,"E10.2.0"),sQuery(id+"F4.wireOp",EDGE,"E10.2.1"),sQuery(id+"F4.wireOp",EDGE,"E10.2.2"),sQuery(id+"F4.wireOp",EDGE,"E10.2.3")])],"isStart":false}),makeQuery(id+"F5.opExtrude","CAP_FACE",FACE,{"disambiguationData":[OSD([sQuery(id+"F4.wireOp",EDGE,"E10.3.0"),sQuery(id+"F4.wireOp",EDGE,"E10.3.1"),sQuery(id+"F4.wireOp",EDGE,"E10.3.2"),sQuery(id+"F4.wireOp",EDGE,"E10.3.3")])],"isStart":false}),makeQuery(id+"F5.opExtrude","CAP_FACE",FACE,{"disambiguationData":[OSD([sQuery(id+"F4.wireOp",EDGE,"E10.4.0"),sQuery(id+"F4.wireOp",EDGE,"E10.4.1"),sQuery(id+"F4.wireOp",EDGE,"E10.4.2"),sQuery(id+"F4.wireOp",EDGE,"E10.4.3")])],"isStart":false}),makeQuery(id+"F5.opExtrude","CAP_FACE",FACE,{"disambiguationData":[OSD([sQuery(id+"F4.wireOp",EDGE,"E10.5.0"),sQuery(id+"F4.wireOp",EDGE,"E10.5.1"),sQuery(id+"F4.wireOp",EDGE,"E10.5.2"),sQuery(id+"F4.wireOp",EDGE,"E10.5.3")])],"isStart":false}),makeQuery(id+"F5.opExtrude","CAP_FACE",FACE,{"disambiguationData":[OSD([sQuery(id+"F4.wireOp",EDGE,"E10.6.0"),sQuery(id+"F4.wireOp",EDGE,"E10.6.1"),sQuery(id+"F4.wireOp",EDGE,"E10.6.2"),sQuery(id+"F4.wireOp",EDGE,"E10.6.3")])],"isStart":false})]});
            var sketch = newSketch(context, id + "F7", { "sketchPlane" : qUnion([Q0])});
            skCircle(sketch, "E13", {"center": v(0, 0) * mm, "radius": 10.75 * mm});
            skSolve(sketch);
        }
        {
            var Q0;
            Q0 = qSketchRegion(id + "F7", true);
            extrude(context, id + "F8", {"entities" : qUnion([Q0]), "operationType" : NewBodyOperationType.REMOVE, "oppositeDirection" : true, "depth" : 1.5 * mm, "offsetDistance" : 25 * mm});
        }
        {
            var Q0;
            Q0=qCreatedBy(makeId("Right.planeOp"),FACE);
            var sketch = newSketch(context, id + "F9", { "sketchPlane" : qUnion([Q0])});
            skLineSegment(sketch, "E14", {"start": v(-7.62, 40) * mm, "end": v(-8.5, 35) * mm});
            skLineSegment(sketch, "E15", {"start": v(-8.5, 35) * mm, "end": v(-1.5, 35) * mm});
            skLineSegment(sketch, "E16", {"start": v(-1.5, 35) * mm, "end": v(-2.38, 40) * mm});
            skLineSegment(sketch, "E17", {"start": v(-2.38, 40) * mm, "end": v(-7.62, 40) * mm});
            skLineSegment(sketch, "E18", {"start": v(0.85, 0) * mm, "end": v(-22.88, 0) * mm, "construction": true});
            skSolve(sketch);
        }
        {
            var Q0;
            Q0 = qSketchRegion(id + "F9", true);
            var Q1;
            Q1=sQuery(id+"F9.wireOp",EDGE,"E18");
            revolve(context, id + "F10", {"operationType" : NewBodyOperationType.REMOVE, "surfaceOperationType" : NewSurfaceOperationType.NEW, "entities" : qUnion([Q0]), "axis" : qUnion([Q1]), "revolveType" : RevolveType.FULL, "oppositeDirection" : true});
        }
    });
